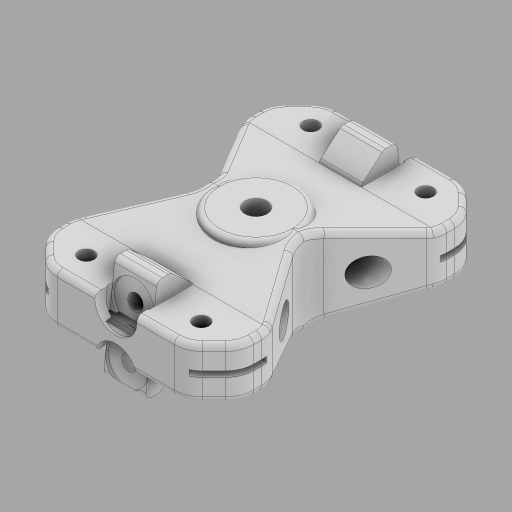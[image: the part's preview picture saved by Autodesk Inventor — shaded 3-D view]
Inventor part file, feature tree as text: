
AUTODESK INVENTOR PART (.ipt)
format: ipt  version: 2023 (Build 270158000, 158)  size: 870,400 bytes
history: native  units: mm
features: extrude x16, fillet x9, sketch x6, chamfer x6, plane x1, loft x1, mirror x1, other x1
ambient origin geometry x8: Origin, YZ Plane, XZ Plane, XY Plane, X Axis, Y Axis, Z Axis, Center Point
bodies: Body1 (feature_tree)
feature tree (41):
  sketch  "Sketch1"  dims[d13=261.822mm d14=7.45mm]
  plane  "Work Plane1"
  sketch  "Sketch2"  dims[d15=27.223mm d17=1.0mm]
  extrude  "Extrusion26"  Depth=7.45mm
  extrude  "Extrusion27"  Depth=1.0mm
  extrude  "Extrusion28"  Depth=35.0mm
  loft  "Loft4"
  extrude  "Extrusion30"  Depth=1.0mm
  extrude  "Extrusion31"  Depth=15.0mm
  extrude  "Extrusion32"  Depth=2.0mm
  extrude  "Extrusion33"  Depth=2.0mm
  sketch  "Sketch13"  dims[d23=2.0mm d25=1.0mm]
  extrude  "Extrusion34"  Depth=1.0mm
  extrude  "Extrusion35"  Depth=2.0mm
  extrude  "Extrusion36"  Depth=10.0mm TaperAngle=0.0deg
  extrude  "Extrusion37"  Depth=2.0mm
  fillet  "Fillet8"  Radius=30.0mm
  extrude  "Extrusion38"  Depth=2.0mm TaperAngle=0.0deg
  chamfer  "Chamfer7"  Distance=8.0mm
  chamfer  "Chamfer8"  Distance=19.96mm
  fillet  "Fillet9"  Radius=15.0mm
  mirror  "Mirror1"
  extrude  "Extrusion39"  TaperAngle=0.0deg  [1 undecoded]
  extrude  "Extrusion40"  TaperAngle=0.0deg  [1 undecoded]
  fillet  "Fillet10"  Radius=2.0mm
  fillet  "Fillet11"  Radius=2.0mm
  extrude  "Extrusion41"  Depth=15.0mm TaperAngle=0.0deg
  extrude  "Extrusion42"  Depth=15.0mm TaperAngle=0.0deg
  chamfer  "Chamfer9"  Distance=15.0mm
  chamfer  "Chamfer10"  Distance=15.0mm
  chamfer  "Chamfer11"  Distance=15.0mm
  chamfer  "Chamfer12"  Distance=15.0mm
  fillet  "Fillet12"  Radius=2.5mm
  fillet  "Fillet13"  Radius=15.0mm
  fillet  "Fillet14"  Radius=15.0mm
  fillet  "Fillet15"  Radius=5.5mm
  fillet  "Fillet16"  Radius=5.5mm
  sketch  "Sketch12"  dims[d21=35.0mm d22=100.0mm]
  other  "Edges5"
  sketch  "Sketch14"  dims[d26=90.0deg d27=1.0mm]
  sketch  "Sketch15"  dims[d28=90.0deg d29=5.5mm d30=15.0mm d31=65.0mm d56=12.0mm d74=1.0mm d75=8.0mm d148=244.423mm d149=41.005864mm d150=244.423mm d151=5.5mm d152=5.5mm d153=5.5mm d154=15.0mm d155=15.0mm d156=18.0mm d157=5.5mm d158=160.0mm d159=10.0mm d160=0.0mm d161=8.0mm d162=30.0mm d163=30.0mm d164=0.0mm d165=8.0mm d166=0.0mm d167=19.96mm d168=15.0mm d169=0.0mm d170=0.0mm d171=90.0deg d172=0.0mm d173=90.0deg d178=2.0mm d179=0.0mm d180=2.0mm d181=15.0mm d182=0.0mm d183=15.0mm d184=0.0mm d185=15.0mm d186=0.0mm d187=15.0mm d188=15.0mm d189=15.0mm d190=2.5mm d191=15.0mm d192=15.0mm d193=5.5mm d194=5.5mm d195=1.0mm d196=0.0mm d197=16.0mm d198=0.0mm d199=15.0mm d200=0.0mm d201=15.0mm d202=0.0mm d203=2.0mm d204=1.0mm d205=0.0mm d206=10.0mm d207=10.0mm d208=45.0deg d209=10.0mm d210=10.0mm d211=45.0deg d212=10.0mm d213=15.0mm d214=0.0mm d215=15.0mm d216=15.0mm d217=0.0mm d218=10.0mm d219=10.0mm d220=30.0mm d221=0.0mm d222=15.0mm d223=10.0mm d224=100.0mm d225=0.0mm d226=8.0mm d227=7.0mm d228=45.0deg d229=7.0mm d230=8.0mm d231=45.0deg d232=12.0mm d233=9.0mm d234=45.0deg d235=9.0mm d236=12.0mm d237=45.0deg d238=2.0mm d239=2.0mm d240=2.0mm d241=2.0mm d242=2.0mm d76=0.5mm d77=0.872665mm d144=0.5mm d145=0.872665mm d146=0.5mm d147=0.872665mm d243=0.0mm d244=0.0mm]
note: 2 required parameter values undecoded (feature->parameter linkage not recoverable at this tier; creation-order binding heuristic only, values carry confidence <= 0.55)
